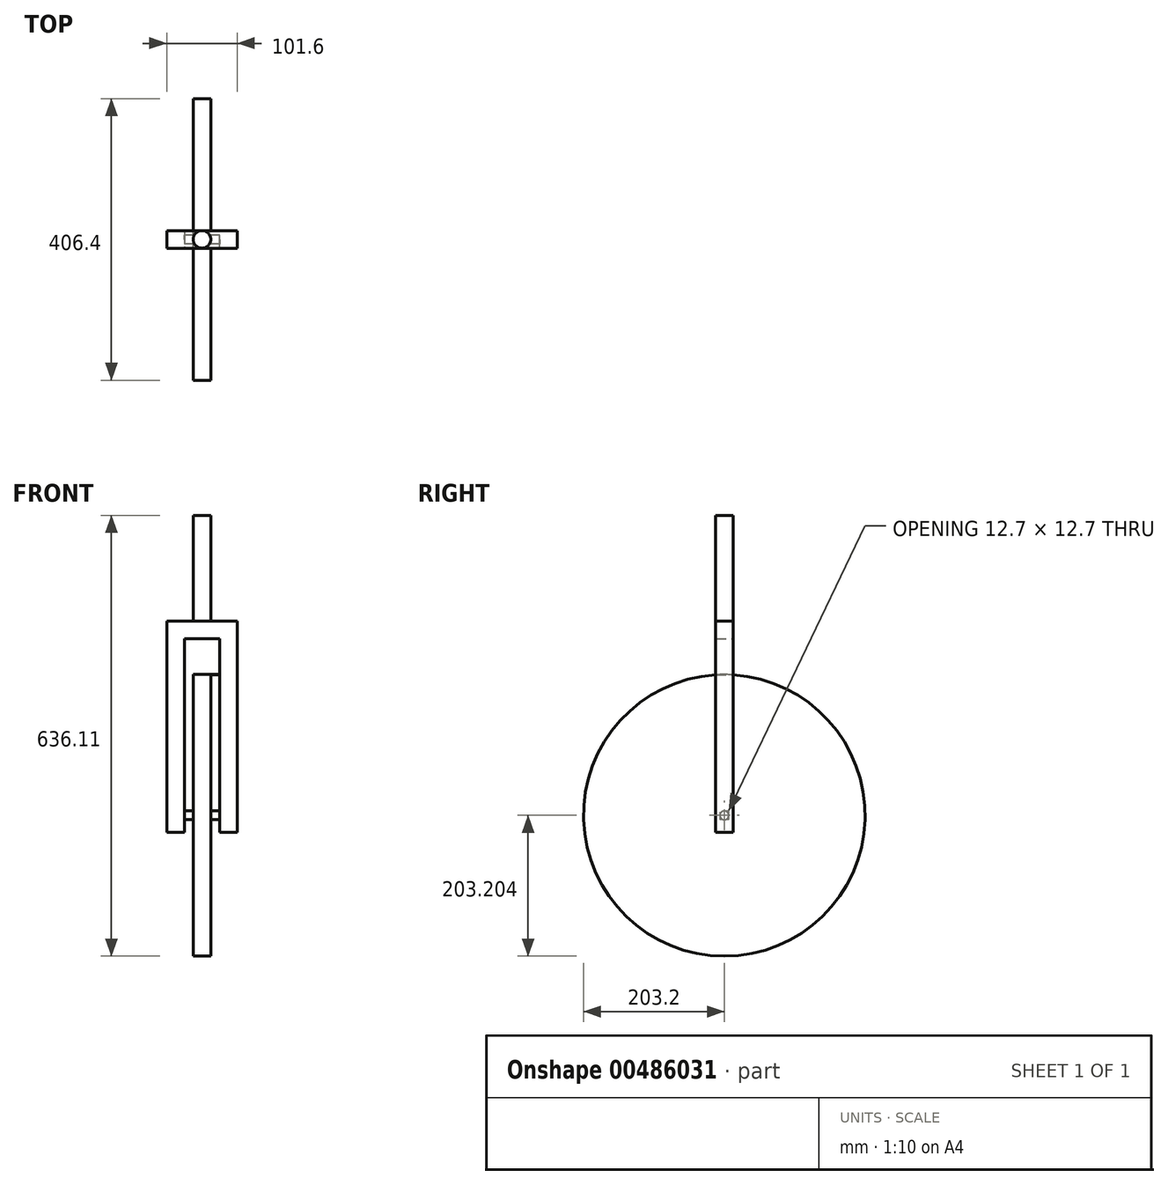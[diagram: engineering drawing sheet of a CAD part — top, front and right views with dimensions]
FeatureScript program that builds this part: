
annotation { "Feature Type Name" : "Feature", "Feature Type Description" : "" }
export const myFeature = defineFeature(function(context is Context, id is Id, definition is map)
    precondition{}
    {
        {
            var Q0;
            Q0=qCreatedBy(makeId("Top.planeOp"),FACE);
            var sketch = newSketch(context, id + "F0", { "sketchPlane" : qUnion([Q0])});
            skLineSegment(sketch, "E0.bottom", {"start": v(0, 0) * mm, "end": v(101.6, 0) * mm});
            skLineSegment(sketch, "E0.top", {"start": v(0, 25.4) * mm, "end": v(101.6, 25.4) * mm});
            skLineSegment(sketch, "E0.left", {"start": v(0, 0) * mm, "end": v(0, 25.4) * mm});
            skLineSegment(sketch, "E0.right", {"start": v(101.6, 0) * mm, "end": v(101.6, 25.4) * mm});
            skSolve(sketch);
        }
        {
            var Q0;
            Q0 = qSketchRegion(id + "F0", true);
            extrude(context, id + "F1", {"entities" : qUnion([Q0]), "depth" : 304.8 * mm, "offsetDistance" : 25.4 * mm});
        }
        {
            var Q0;
            Q0=makeQuery(id+"F1.opExtrude","CAP_FACE",FACE,{"disambiguationData":[OSD([sQuery(id+"F0.wireOp",EDGE,"E0.bottom"),sQuery(id+"F0.wireOp",EDGE,"E0.top"),sQuery(id+"F0.wireOp",EDGE,"E0.left"),sQuery(id+"F0.wireOp",EDGE,"E0.right")])],"isStart":true});
            var sketch = newSketch(context, id + "F2", { "sketchPlane" : qUnion([Q0])});
            skLineSegment(sketch, "E1.bottom", {"start": v(0, 0) * mm, "end": v(101.6, 0) * mm});
            skLineSegment(sketch, "E1.top", {"start": v(0, -25.4) * mm, "end": v(101.6, -25.4) * mm});
            skLineSegment(sketch, "E1.left", {"start": v(0, 0) * mm, "end": v(0, -25.4) * mm});
            skLineSegment(sketch, "E1.right", {"start": v(101.6, 0) * mm, "end": v(101.6, -25.4) * mm});
            skLineSegment(sketch, "E2", {"start": v(0, 0) * mm, "end": v(50.8, 0) * mm});
            skLineSegment(sketch, "E3", {"start": v(50.8, 0) * mm, "end": v(101.6, 0) * mm});
            skLineSegment(sketch, "E4", {"start": v(76.2, 0) * mm, "end": v(76.2, -25.4) * mm});
            skLineSegment(sketch, "E5", {"start": v(76.26, -25.34) * mm, "end": v(25.4, -25.4) * mm});
            skPoint(sketch, "E5.endSnap0", {"position": v(25.4, 0) * mm});
            skLineSegment(sketch, "E6", {"start": v(25.4, -25.4) * mm, "end": v(25.4, 0) * mm});
            skSolve(sketch);
        }
        {
            var Q0;
            {var subQ0=sQuery(id+"F2.wireOp",EDGE,"E4");var subQ1=sQuery(id+"F2.wireOp",EDGE,"E1.top");var subQ2=makeQuery(id+"F2.imprint","INTERSECT",VERTEX,{"derivedFrom":[subQ1,subQ0]});Q0=makeQuery(id+"F2.imprint","IMPRINT",FACE,{"disambiguationData":[TD([[makeQuery(id+"F2.imprint","IMPRINT",EDGE,{"disambiguationData":[TD([[subQ2,1.0]])],"derivedFrom":subQ0}),-1.0]])]});}
            var Q1;
            {var subQ7=sQuery(id+"F2.wireOp",EDGE,"E6");Q1=makeQuery(id+"F2.imprint","IMPRINT",FACE,{"disambiguationData":[TD([[makeQuery(id+"F2.imprint","IMPRINT",EDGE,{"derivedFrom":subQ7}),-1.0]])]});}
            extrude(context, id + "F3", {"entities" : qUnion([Q0, Q1]), "operationType" : NewBodyOperationType.REMOVE, "oppositeDirection" : true, "depth" : 279.4 * mm, "offsetDistance" : 25.4 * mm});
        }
        {
            var Q0;
            Q0=makeQuery(id+"F1.opExtrude","CAP_FACE",FACE,{"disambiguationData":[OSD([sQuery(id+"F0.wireOp",EDGE,"E0.bottom"),sQuery(id+"F0.wireOp",EDGE,"E0.top"),sQuery(id+"F0.wireOp",EDGE,"E0.left"),sQuery(id+"F0.wireOp",EDGE,"E0.right")])],"isStart":false});
            var sketch = newSketch(context, id + "F4", { "sketchPlane" : qUnion([Q0])});
            skCircle(sketch, "E7", {"center": v(50.8, 12.7) * mm, "radius": 12.7 * mm});
            skSolve(sketch);
        }
        {
            var Q0;
            Q0 = qSketchRegion(id + "F4", true);
            extrude(context, id + "F5", {"entities" : qUnion([Q0]), "operationType" : NewBodyOperationType.ADD, "depth" : 152.4 * mm, "offsetDistance" : 25.4 * mm});
        }
        {
            var Q0;
            Q0=makeQuery(id+"F3.boolean.opBoolean","COPY",FACE,{"derivedFrom":makeQuery(id+"F3.opExtrude","SWEPT_FACE",FACE,{"disambiguationData":[OSD([sQuery(id+"F2.wireOp",EDGE,"E4")])]})});
            var sketch = newSketch(context, id + "F6", { "sketchPlane" : qUnion([Q0])});
            skLineSegment(sketch, "E8.bottom", {"start": v(0, 0) * mm, "end": v(-25.4, 0) * mm});
            skLineSegment(sketch, "E8.top", {"start": v(0, 48.59) * mm, "end": v(-25.4, 48.59) * mm});
            skLineSegment(sketch, "E8.left", {"start": v(0, 0) * mm, "end": v(0, 48.59) * mm});
            skLineSegment(sketch, "E8.right", {"start": v(-25.4, 0) * mm, "end": v(-25.4, 48.59) * mm});
            skLineSegment(sketch, "E9", {"start": v(-25.4, 48.59) * mm, "end": v(0, 0) * mm});
            skCircle(sketch, "E10", {"center": v(-12.7, 24.3) * mm, "radius": 203.2 * mm});
            skSolve(sketch);
        }
        {
            var Q0;
            Q0 = qSketchRegion(id + "F6", true);
            var Q1;
            Q1=makeQuery(id+"F6.imprint","IMPRINT",FACE,{"disambiguationData":[TD([[makeQuery(id+"F6.imprint","IMPRINT",EDGE,{"derivedFrom":sQuery(id+"F6.wireOp",EDGE,"E8.bottom")}),-1.0]])]});
            var Q2;
            Q2=makeQuery(id+"F6.imprint","IMPRINT",FACE,{"disambiguationData":[TD([[makeQuery(id+"F6.imprint","IMPRINT",EDGE,{"derivedFrom":sQuery(id+"F6.wireOp",EDGE,"E8.top")}),1.0]])]});
            extrude(context, id + "F7", {"entities" : qUnion([Q0, Q1, Q2]), "operationType" : NewBodyOperationType.ADD, "depth" : 38.1 * mm, "offsetDistance" : 25.4 * mm});
        }
        {
            var Q0;
            Q0=makeQuery(id+"F7.opExtrude","CAP_FACE",FACE,{"disambiguationData":[OSD([sQuery(id+"F6.wireOp",EDGE,"E10")])],"isStart":true});
            extrude(context, id + "F8", {"entities" : qUnion([Q0]), "operationType" : NewBodyOperationType.REMOVE, "oppositeDirection" : true, "depth" : 12.7 * mm, "offsetDistance" : 25.4 * mm});
        }
        {
            var Q0;
            Q0=makeQuery(id+"F8.boolean.opBoolean","MERGE",FACE,{"derivedFrom":[makeQuery(id+"F1.opExtrude","SWEPT_FACE",FACE,{"disambiguationData":[OSD([sQuery(id+"F0.wireOp",EDGE,"E0.top")])]}),makeQuery(id+"F8.opExtrude","SWEPT_FACE",FACE,{"disambiguationData":[OSD([sQuery(id+"F2.wireOp",EDGE,"E1.top"),sQuery(id+"F2.wireOp",EDGE,"E4")])]})]});
            var sketch = newSketch(context, id + "F9", { "sketchPlane" : qUnion([Q0])});
            skLineSegment(sketch, "E11.bottom", {"start": v(-76.2, 227.1) * mm, "end": v(-63.5, 227.1) * mm});
            skLineSegment(sketch, "E11.top", {"start": v(-76.2, 0) * mm, "end": v(-63.5, 0) * mm});
            skLineSegment(sketch, "E11.left", {"start": v(-76.2, 227.1) * mm, "end": v(-76.2, 0) * mm});
            skLineSegment(sketch, "E11.right", {"start": v(-63.5, 227.1) * mm, "end": v(-63.5, 0) * mm});
            skSolve(sketch);
        }
        {
            var Q0;
            Q0 = qSketchRegion(id + "F9", true);
            extrude(context, id + "F10", {"entities" : qUnion([Q0]), "operationType" : NewBodyOperationType.REMOVE, "oppositeDirection" : true, "depth" : 25.4 * mm, "offsetDistance" : 25.4 * mm});
        }
        {
            var Q0;
            Q0=makeQuery(id+"F10.boolean.opBoolean","MERGE",FACE,{"derivedFrom":[makeQuery(id+"F8.boolean.opBoolean","COPY",FACE,{"derivedFrom":makeQuery(id+"F8.opExtrude","CAP_FACE",FACE,{"disambiguationData":[OSD([sQuery(id+"F6.wireOp",EDGE,"E10")])],"isStart":false})}),makeQuery(id+"F10.opExtrude","SWEPT_FACE",FACE,{"disambiguationData":[OSD([sQuery(id+"F9.wireOp",EDGE,"E11.right")])]})]});
            var sketch = newSketch(context, id + "F11", { "sketchPlane" : qUnion([Q0])});
            skCircle(sketch, "E12", {"center": v(12.7, 24.3) * mm, "radius": 6.35 * mm});
            skSolve(sketch);
        }
        {
            var Q0;
            Q0 = qSketchRegion(id + "F11", true);
            extrude(context, id + "F12", {"entities" : qUnion([Q0]), "operationType" : NewBodyOperationType.ADD, "depth" : 25.4 * mm, "offsetDistance" : 25.4 * mm, "hasSecondDirection" : true, "secondDirectionOppositeDirection" : true, "secondDirectionDepth" : 50.8 * mm});
        }
    });
